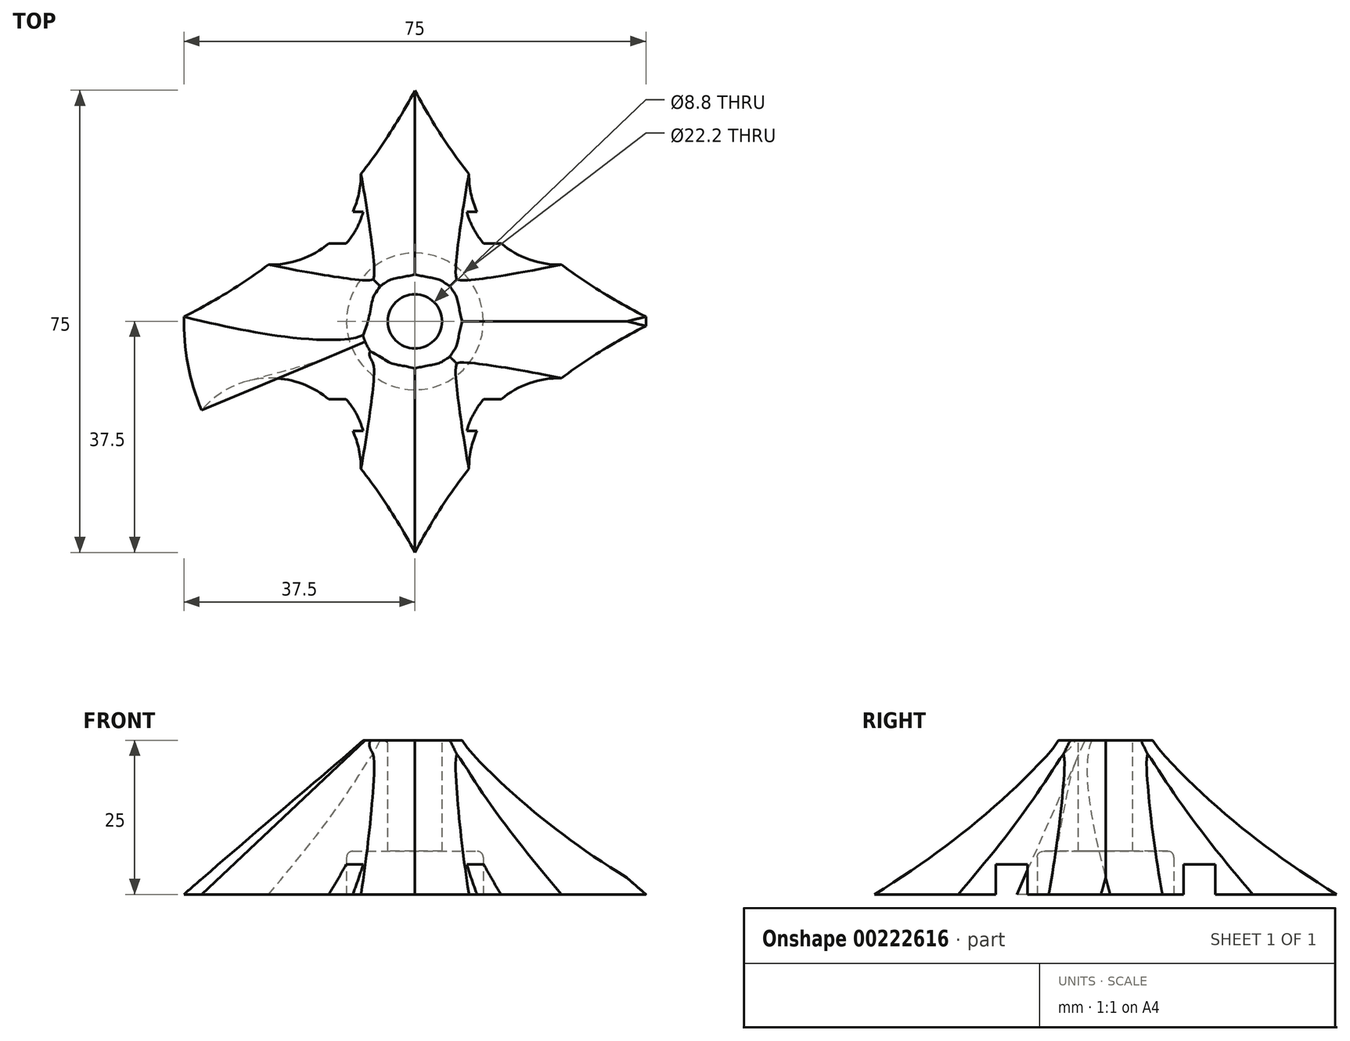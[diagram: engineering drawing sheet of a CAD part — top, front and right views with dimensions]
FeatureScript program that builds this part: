
annotation { "Feature Type Name" : "Feature", "Feature Type Description" : "" }
export const myFeature = defineFeature(function(context is Context, id is Id, definition is map)
    precondition{}
    {
        {
            var Q0;
            Q0=qCreatedBy(makeId("Top.planeOp"),FACE);
            cPlane(context, id + "F0", {"entities" : qUnion([Q0]), "cplaneType" : CPlaneType.OFFSET, "offset" : 25 * mm, "width" : 150 * mm, "height" : 150 * mm});
        }
        {
            var Q0;
            Q0=qCreatedBy(makeId("Top.planeOp"),FACE);
            var sketch = newSketch(context, id + "F1", { "sketchPlane" : qUnion([Q0])});
            skArc(sketch, "E0", {"start": v(-34.62, 14.4) * mm, "mid": v(-37.5, 0) * mm, "end": v(-34.62, -14.4) * mm});
            skArc(sketch, "E1", {"start": v(-34.62, 14.4) * mm, "mid": v(-13.16, 13.4) * mm, "end": v(-13.75, 34.89) * mm});
            skArc(sketch, "E2.MirrorCS", {"start": v(34.62, 14.4) * mm, "mid": v(13.16, 13.4) * mm, "end": v(13.75, 34.89) * mm});
            skArc(sketch, "E3.MirrorCS", {"start": v(34.62, -14.4) * mm, "mid": v(13.16, -13.4) * mm, "end": v(13.75, -34.89) * mm});
            skArc(sketch, "E4.MirrorCS", {"start": v(-34.62, -14.4) * mm, "mid": v(-13.16, -13.4) * mm, "end": v(-13.75, -34.89) * mm});
            skArc(sketch, "E5.trimOffspring", {"start": v(13.75, 34.89) * mm, "mid": v(0, 37.5) * mm, "end": v(-13.75, 34.89) * mm});
            skArc(sketch, "E6.trimOffspring", {"start": v(34.62, -14.4) * mm, "mid": v(37.5, 0) * mm, "end": v(34.62, 14.4) * mm});
            skArc(sketch, "E7.trimOffspring", {"start": v(-13.75, -34.89) * mm, "mid": v(0, -37.5) * mm, "end": v(13.75, -34.89) * mm});
            skSolve(sketch);
        }
        {
            var Q0;
            Q0=qCreatedBy(id+"F0.planeOp",FACE);
            var sketch = newSketch(context, id + "F2", { "sketchPlane" : qUnion([Q0])});
            skCircle(sketch, "E8", {"center": v(0, 0) * mm, "radius": 8.72 * mm});
            skSolve(sketch);
        }
        {
            var Q0;
            Q0=makeQuery(id+"F1.imprint","IMPRINT",FACE,{"disambiguationData":[TD([[makeQuery(id+"F1.imprint","IMPRINT",EDGE,{"derivedFrom":sQuery(id+"F1.wireOp",EDGE,"E0")}),1.0]])]});
            var Q1;
            Q1=makeQuery(id+"F2.imprint","IMPRINT",FACE,{"disambiguationData":[TD([[makeQuery(id+"F2.imprint","IMPRINT",EDGE,{"derivedFrom":sQuery(id+"F2.wireOp",EDGE,"E8")}),1.0]])]});
            loft(context, id + "F3", {"sheetProfilesArray" : [{ "sheetProfileEntities" : qUnion([Q0]) }, { "sheetProfileEntities" : qUnion([Q1]) }]});
        }
        {
            var Q0;
            Q0=sQuery(id+"F2.wireOp",VERTEX,"E8.center");
            var Q1;
            Q1=makeQuery(id+"F3.opLoft","SWEPT_BODY",BODY,{"disambiguationData":[OSD([makeQuery(id+"F1.imprint","IMPRINT",FACE,{"disambiguationData":[TD([[makeQuery(id+"F1.imprint","IMPRINT",EDGE,{"derivedFrom":sQuery(id+"F1.wireOp",EDGE,"8nXoAvfi-UBXD-KZsx-itxO-UelUVCI2CAJj")}),-1.0]])]}),makeQuery(id+"F2.imprint","IMPRINT",FACE,{"disambiguationData":[TD([[makeQuery(id+"F2.imprint","IMPRINT",EDGE,{"derivedFrom":sQuery(id+"F2.wireOp",EDGE,"E8")}),1.0]])]})])]});
            hole(context, id + "F4", {"style" : HoleStyle.SIMPLE, "endStyle" : HoleEndStyle.THROUGH, "standardTappedOrClearance" : lookupTablePath({ "standard" : "ISO", "fit" : "Normal", "size" : "M8", "type" : "Clearance" }), "standardBlindInLast" : lookupTablePath({ "fit" : "Standard", "standard" : "ISO", "size" : "M8", "type" : "Clearance" }), "holeDiameter" : 8.8 * mm, "isTappedThrough" : true, "tappedDepth" : 12 * mm, "tapClearance" : 3, "startFromSketch" : true, "locations" : qUnion([Q0]), "scope" : qUnion([Q1])});
        }
        {
            var Q0;
            Q0=makeQuery(id+"F3.opLoft","CAP_FACE",FACE,{"disambiguationData":[OSD([makeQuery(id+"F1.imprint","IMPRINT",FACE,{"disambiguationData":[TD([[makeQuery(id+"F1.imprint","IMPRINT",EDGE,{"derivedFrom":sQuery(id+"F1.wireOp",EDGE,"E0")}),1.0]])]})])],"isStart":true});
            var sketch = newSketch(context, id + "F5", { "sketchPlane" : qUnion([Q0])});
            skCircle(sketch, "E9", {"center": v(0, 0) * mm, "radius": 11.1 * mm});
            skSolve(sketch);
        }
        {
            var Q0;
            Q0=makeQuery(id+"F5.imprint","IMPRINT",FACE,{"disambiguationData":[TD([[makeQuery(id+"F5.imprint","IMPRINT",EDGE,{"derivedFrom":sQuery(id+"F5.wireOp",EDGE,"E9")}),1.0]])]});
            var Q1;
            Q1=sQuery(id+"F5.wireOp",EDGE,"E9");
            extrude(context, id + "F6", {"entities" : qUnion([Q0]), "operationType" : NewBodyOperationType.REMOVE, "surfaceEntities" : qUnion([Q1]), "oppositeDirection" : true, "depth" : 7 * mm});
        }
        {
            var Q0;
            Q0=makeQuery(id+"F6.boolean.opBoolean","COPY",EDGE,{"derivedFrom":makeQuery(id+"F6.opExtrude","CAP_EDGE",EDGE,{"disambiguationData":[OSD([sQuery(id+"F5.wireOp",EDGE,"E9")])],"isStart":false})});
            fillet(context, id + "F7", {"entities" : qUnion([Q0]), "radius" : 1 * mm, "tangentPropagation" : true, "allowEdgeOverflow" : false});
        }
        {
            var Q0;
            Q0=makeQuery(id+"F3.opLoft","SWEPT_EDGE",EDGE,{"disambiguationData":[OSD([sQuery(id+"F1.wireOp",EDGE,"E2.MirrorCS"),sQuery(id+"F1.wireOp",EDGE,"E5.trimOffspring"),sQuery(id+"F1.wireOp",EDGE,"E6.trimOffspring"),sQuery(id+"F2.wireOp",EDGE,"E8")])]});
            var Q1;
            Q1=makeQuery(id+"F3.opLoft","SWEPT_EDGE",EDGE,{"disambiguationData":[OSD([sQuery(id+"F1.wireOp",EDGE,"E1"),sQuery(id+"F1.wireOp",EDGE,"E2.MirrorCS"),sQuery(id+"F1.wireOp",EDGE,"E5.trimOffspring"),sQuery(id+"F2.wireOp",EDGE,"E8")])]});
            var Q2;
            Q2=makeQuery(id+"F3.opLoft","SWEPT_EDGE",EDGE,{"disambiguationData":[OSD([sQuery(id+"F1.wireOp",EDGE,"E0"),sQuery(id+"F1.wireOp",EDGE,"E1")])]});
            var Q3;
            Q3=makeQuery(id+"F3.opLoft","SWEPT_EDGE",EDGE,{"disambiguationData":[OSD([sQuery(id+"F1.wireOp",EDGE,"E0"),sQuery(id+"F1.wireOp",EDGE,"E1"),sQuery(id+"F1.wireOp",EDGE,"E4.MirrorCS"),sQuery(id+"F2.wireOp",EDGE,"E8")])]});
            var Q4;
            Q4=makeQuery(id+"F3.opLoft","SWEPT_EDGE",EDGE,{"disambiguationData":[OSD([sQuery(id+"F1.wireOp",EDGE,"E0"),sQuery(id+"F1.wireOp",EDGE,"E4.MirrorCS"),sQuery(id+"F1.wireOp",EDGE,"E7.trimOffspring"),sQuery(id+"F2.wireOp",EDGE,"E8")])]});
            var Q5;
            Q5=makeQuery(id+"F3.opLoft","SWEPT_EDGE",EDGE,{"disambiguationData":[OSD([sQuery(id+"F1.wireOp",EDGE,"E3.MirrorCS"),sQuery(id+"F1.wireOp",EDGE,"E4.MirrorCS"),sQuery(id+"F1.wireOp",EDGE,"E7.trimOffspring"),sQuery(id+"F2.wireOp",EDGE,"E8")])]});
            var Q6;
            Q6=makeQuery(id+"F3.opLoft","SWEPT_EDGE",EDGE,{"disambiguationData":[OSD([sQuery(id+"F1.wireOp",EDGE,"E3.MirrorCS"),sQuery(id+"F1.wireOp",EDGE,"E6.trimOffspring"),sQuery(id+"F1.wireOp",EDGE,"E7.trimOffspring"),sQuery(id+"F2.wireOp",EDGE,"E8")])]});
            var Q7;
            Q7=makeQuery(id+"F3.opLoft","SWEPT_EDGE",EDGE,{"disambiguationData":[OSD([sQuery(id+"F1.wireOp",EDGE,"E2.MirrorCS"),sQuery(id+"F1.wireOp",EDGE,"E3.MirrorCS"),sQuery(id+"F1.wireOp",EDGE,"E6.trimOffspring"),sQuery(id+"F2.wireOp",EDGE,"E8")])]});
            chamfer(context, id + "F8", {"entities" : qUnion([Q0, Q1, Q2, Q3, Q4, Q5, Q6, Q7]), "width" : 10 * mm, "tangentPropagation" : true});
        }
        {
            var Q0;
            Q0=qCreatedBy(makeId("Right.planeOp"),FACE);
            var sketch = newSketch(context, id + "F9", { "sketchPlane" : qUnion([Q0])});
            skLineSegment(sketch, "E10.bottom", {"start": v(17.8, 0) * mm, "end": v(12.65, 0) * mm});
            skLineSegment(sketch, "E10.top", {"start": v(17.8, 4.88) * mm, "end": v(12.65, 4.88) * mm});
            skLineSegment(sketch, "E10.left", {"start": v(17.8, 0) * mm, "end": v(17.8, 4.88) * mm});
            skLineSegment(sketch, "E10.right", {"start": v(12.65, 0) * mm, "end": v(12.65, 4.88) * mm});
            skLineSegment(sketch, "E11.MirrorCS", {"start": v(-12.65, 0) * mm, "end": v(-12.65, 4.88) * mm});
            skLineSegment(sketch, "E12.MirrorCS", {"start": v(-17.8, 0) * mm, "end": v(-12.65, 0) * mm});
            skLineSegment(sketch, "E13.MirrorCS", {"start": v(-17.8, 4.88) * mm, "end": v(-12.65, 4.88) * mm});
            skLineSegment(sketch, "E14.MirrorCS", {"start": v(-17.8, 0) * mm, "end": v(-17.8, 4.88) * mm});
            skSolve(sketch);
        }
        {
            var Q0;
            Q0 = qSketchRegion(id + "F9", true);
            extrude(context, id + "F10", {"entities" : qUnion([Q0]), "operationType" : NewBodyOperationType.REMOVE, "oppositeDirection" : true, "depth" : 25 * mm, "hasSecondDirection" : true, "secondDirectionOppositeDirection" : false, "secondDirectionDepth" : 25 * mm});
        }
    });
